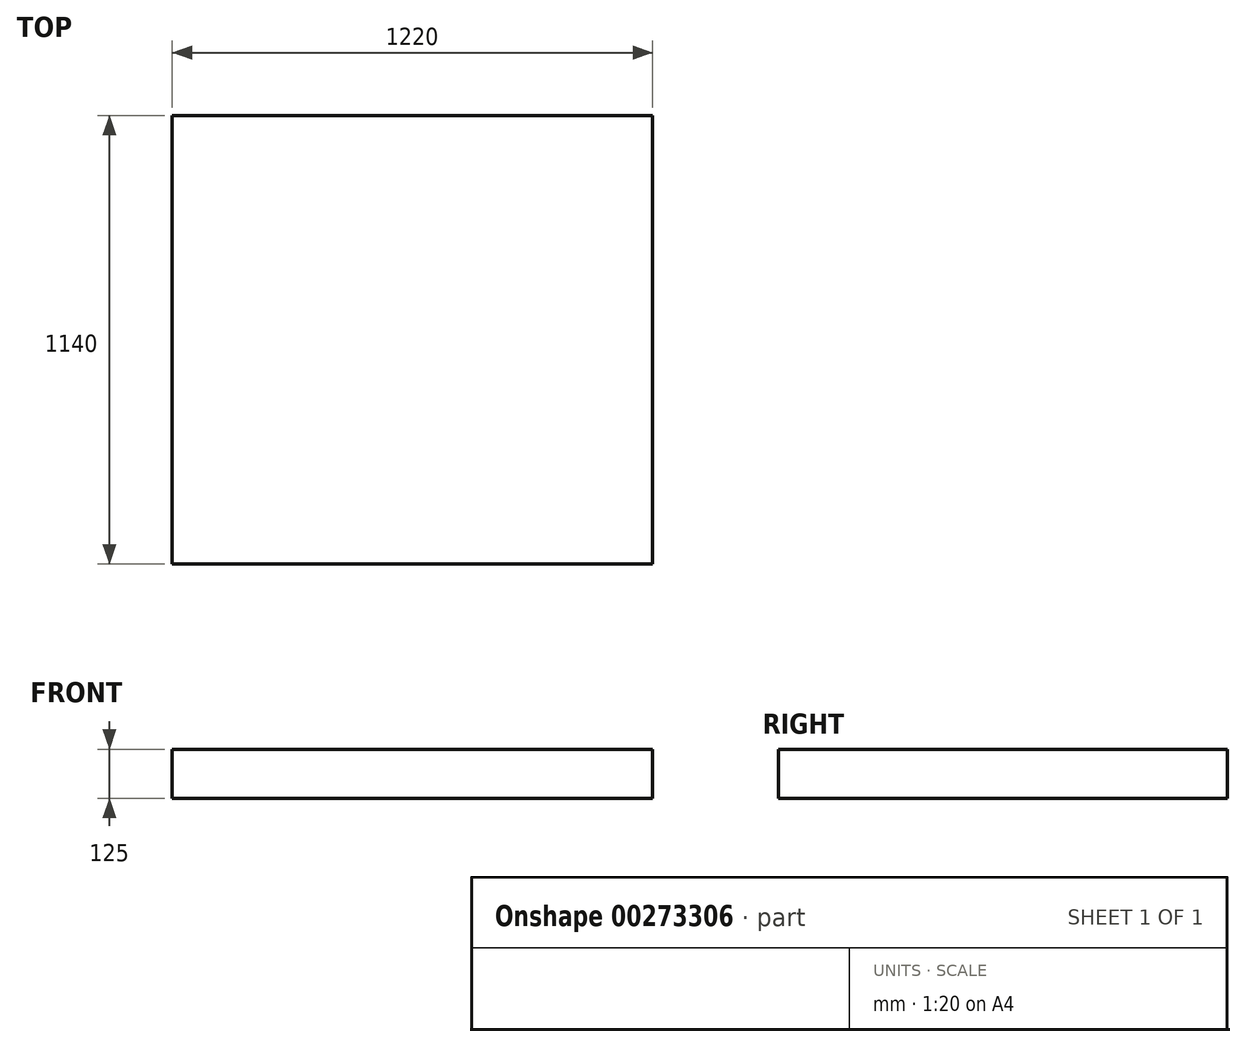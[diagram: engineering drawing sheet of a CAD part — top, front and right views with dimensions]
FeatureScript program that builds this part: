
annotation { "Feature Type Name" : "Feature", "Feature Type Description" : "" }
export const myFeature = defineFeature(function(context is Context, id is Id, definition is map)
    precondition{}
    {
        {
            var Q0;
            Q0=qCreatedBy(makeId("Top.planeOp"),FACE);
            var sketch = newSketch(context, id + "F0", { "sketchPlane" : qUnion([Q0])});
            skLineSegment(sketch, "E0.bottom", {"start": v(0, 0) * mm, "end": v(1220, 0) * mm});
            skLineSegment(sketch, "E0.top", {"start": v(0, 1140) * mm, "end": v(1220, 1140) * mm});
            skLineSegment(sketch, "E0.left", {"start": v(0, 0) * mm, "end": v(0, 1140) * mm});
            skLineSegment(sketch, "E0.right", {"start": v(1220, 0) * mm, "end": v(1220, 1140) * mm});
            skLineSegment(sketch, "E1.bottom", {"start": v(74.23, 31.32) * mm, "end": v(-87.1, 31.32) * mm});
            skLineSegment(sketch, "E1.top", {"start": v(74.23, -116.63) * mm, "end": v(-87.1, -116.63) * mm});
            skLineSegment(sketch, "E1.left", {"start": v(74.23, 31.32) * mm, "end": v(74.23, -116.63) * mm});
            skLineSegment(sketch, "E1.right", {"start": v(-87.1, 31.32) * mm, "end": v(-87.1, -116.63) * mm});
            skSolve(sketch);
        }
        {
            var Q0;
            {var subQ2=sQuery(id+"F0.wireOp",EDGE,"E0.top");Q0=makeQuery(id+"F0.imprint","IMPRINT",FACE,{"disambiguationData":[TD([[makeQuery(id+"F0.imprint","IMPRINT",EDGE,{"derivedFrom":subQ2}),-1.0]])]});}
            var Q1;
            {var subQ0=sQuery(id+"F0.wireOp",EDGE,"E0.left");var subQ1=sQuery(id+"F0.wireOp",EDGE,"E0.bottom");var subQ2=makeQuery(id+"F0.imprint","INTERSECT",VERTEX,{"derivedFrom":[subQ1,subQ0]});Q1=makeQuery(id+"F0.imprint","IMPRINT",FACE,{"disambiguationData":[TD([[makeQuery(id+"F0.imprint","IMPRINT",EDGE,{"disambiguationData":[TD([[subQ2,-1.0]])],"derivedFrom":subQ1}),1.0]])]});}
            extrude(context, id + "F1", {"entities" : qUnion([Q0, Q1]), "depth" : 125 * mm});
        }
    });
